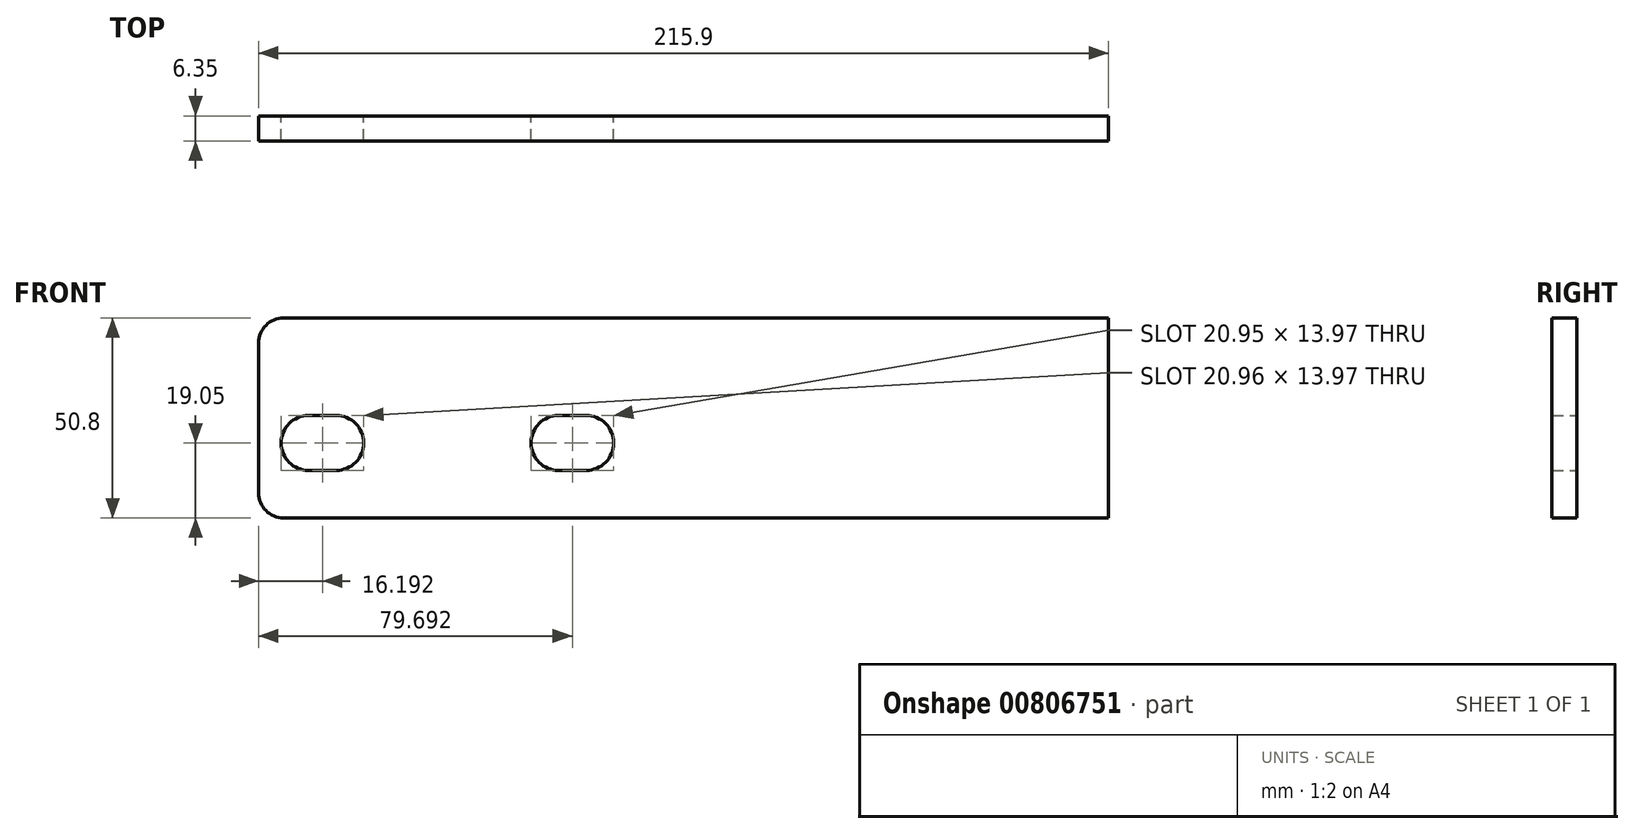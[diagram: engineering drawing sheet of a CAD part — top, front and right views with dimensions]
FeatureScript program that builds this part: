
annotation { "Feature Type Name" : "Feature", "Feature Type Description" : "" }
export const myFeature = defineFeature(function(context is Context, id is Id, definition is map)
    precondition{}
    {
        {
            var Q0;
            Q0=qCreatedBy(makeId("Front.planeOp"),FACE);
            var sketch = newSketch(context, id + "F0", { "sketchPlane" : qUnion([Q0])});
            skLineSegment(sketch, "E0.bottom", {"start": v(-44.45, -50.8) * mm, "end": v(165.1, -50.8) * mm});
            skLineSegment(sketch, "E0.top", {"start": v(-44.45, 0) * mm, "end": v(165.1, 0) * mm});
            skLineSegment(sketch, "E0.left", {"start": v(-50.8, -44.45) * mm, "end": v(-50.8, -6.35) * mm});
            skLineSegment(sketch, "E0.right", {"start": v(165.1, -50.8) * mm, "end": v(165.1, 0) * mm});
            skArc(sketch, "E1", {"start": v(-38.1, -24.77) * mm, "mid": v(-45.09, -31.75) * mm, "end": v(-38.1, -38.74) * mm});
            skArc(sketch, "E2", {"start": v(25.4, -24.77) * mm, "mid": v(18.41, -31.75) * mm, "end": v(25.4, -38.74) * mm});
            skArc(sketch, "E3", {"start": v(32.39, -38.74) * mm, "mid": v(39.37, -31.75) * mm, "end": v(32.39, -24.77) * mm});
            skArc(sketch, "E4", {"start": v(-31.12, -38.74) * mm, "mid": v(-24.13, -31.75) * mm, "end": v(-31.12, -24.77) * mm});
            skLineSegment(sketch, "E5", {"start": v(32.39, -24.77) * mm, "end": v(25.4, -24.77) * mm});
            skLineSegment(sketch, "E6", {"start": v(32.39, -38.74) * mm, "end": v(25.4, -38.74) * mm});
            skLineSegment(sketch, "E7", {"start": v(-31.12, -24.77) * mm, "end": v(-38.1, -24.77) * mm});
            skLineSegment(sketch, "E8", {"start": v(-31.12, -38.74) * mm, "end": v(-38.1, -38.74) * mm});
            skPoint(sketch, "E9.visualSharp", {"position": v(-50.8, 0) * mm});
            skArc(sketch, "E9.filletArc", {"start": v(-44.45, 0) * mm, "mid": v(-48.94, -1.86) * mm, "end": v(-50.8, -6.35) * mm});
            skPoint(sketch, "E10.visualSharp", {"position": v(-50.8, -50.8) * mm});
            skArc(sketch, "E10.filletArc", {"start": v(-50.8, -44.45) * mm, "mid": v(-48.94, -48.94) * mm, "end": v(-44.45, -50.8) * mm});
            skSolve(sketch);
        }
        {
            var Q0;
            Q0 = qSketchRegion(id + "F0", true);
            extrude(context, id + "F1", {"entities" : qUnion([Q0]), "depth" : 6.35 * mm, "offsetDistance" : 25.4 * mm});
        }
    });
